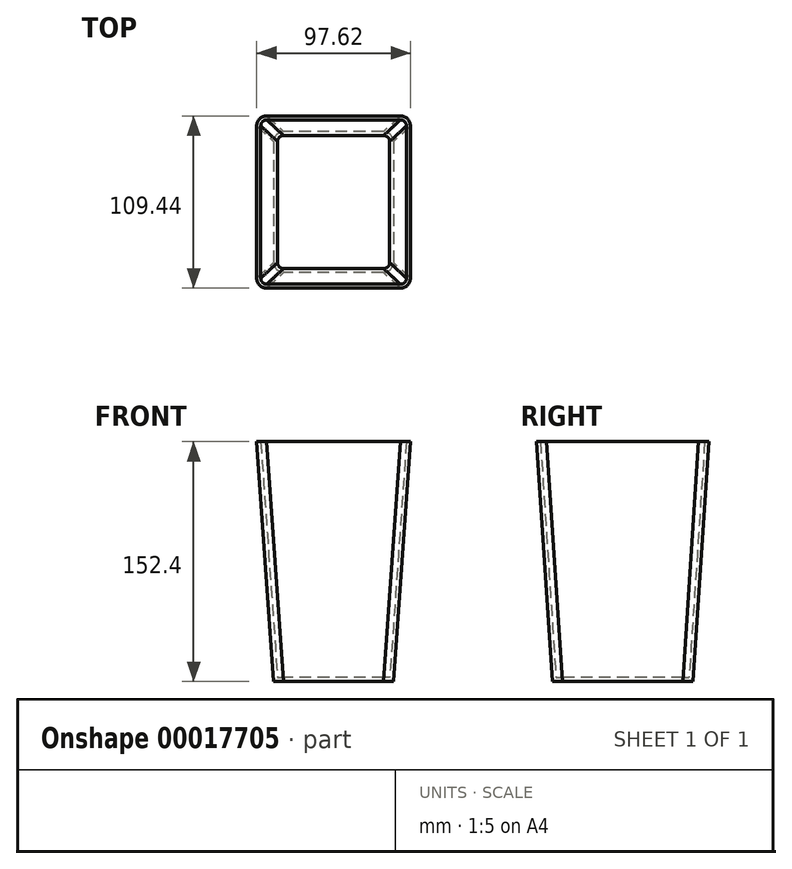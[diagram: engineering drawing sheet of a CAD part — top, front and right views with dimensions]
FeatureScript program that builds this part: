
annotation { "Feature Type Name" : "Feature", "Feature Type Description" : "" }
export const myFeature = defineFeature(function(context is Context, id is Id, definition is map)
    precondition{}
    {
        {
            var Q0;
            Q0=qCreatedBy(makeId("Top.planeOp"),FACE);
            var sketch = newSketch(context, id + "F0", { "sketchPlane" : qUnion([Q0])});
            skLineSegment(sketch, "E0.rect.bottom", {"start": v(31.64, 44.66) * mm, "end": v(-31.64, 44.66) * mm});
            skLineSegment(sketch, "E0.rect.top", {"start": v(31.64, -44.66) * mm, "end": v(-31.64, -44.66) * mm});
            skLineSegment(sketch, "E0.rect.left", {"start": v(38, 38.3) * mm, "end": v(38, -38.3) * mm});
            skLineSegment(sketch, "E0.rect.right", {"start": v(-38, 38.3) * mm, "end": v(-38, -38.3) * mm});
            skPoint(sketch, "E0.rect.middle", {"position": v(0, 0) * mm});
            skPoint(sketch, "E1.visualSharp", {"position": v(-38, 44.66) * mm});
            skArc(sketch, "E1.filletArc", {"start": v(-31.64, 44.66) * mm, "mid": v(-36.13, 42.8) * mm, "end": v(-38, 38.3) * mm});
            skPoint(sketch, "E2.visualSharp", {"position": v(38, 44.66) * mm});
            skArc(sketch, "E2.filletArc", {"start": v(38, 38.3) * mm, "mid": v(36.13, 42.8) * mm, "end": v(31.64, 44.66) * mm});
            skPoint(sketch, "E3.visualSharp", {"position": v(38, -44.66) * mm});
            skArc(sketch, "E3.filletArc", {"start": v(31.64, -44.66) * mm, "mid": v(36.13, -42.8) * mm, "end": v(38, -38.3) * mm});
            skPoint(sketch, "E4.visualSharp", {"position": v(-38, -44.66) * mm});
            skArc(sketch, "E4.filletArc", {"start": v(-38, -38.3) * mm, "mid": v(-36.13, -42.8) * mm, "end": v(-31.64, -44.66) * mm});
            skSolve(sketch);
        }
        {
            var Q0;
            Q0=makeQuery(id+"F0.imprint","IMPRINT",FACE,{"disambiguationData":[TD([[makeQuery(id+"F0.imprint","IMPRINT",EDGE,{"derivedFrom":sQuery(id+"F0.wireOp",EDGE,"E0.rect.bottom")}),1.0]])]});
            cPlane(context, id + "F1", {"entities" : qUnion([Q0]), "cplaneType" : CPlaneType.OFFSET, "offset" : 152.4 * mm, "width" : 152.4 * mm, "height" : 152.4 * mm});
        }
        {
            var Q0;
            Q0=qCreatedBy(id+"F1.planeOp",FACE);
            var sketch = newSketch(context, id + "F2", { "sketchPlane" : qUnion([Q0])});
            skLineSegment(sketch, "E5.rect.bottom", {"start": v(42.46, 54.72) * mm, "end": v(-42.46, 54.72) * mm});
            skLineSegment(sketch, "E5.rect.top", {"start": v(42.46, -54.72) * mm, "end": v(-42.46, -54.72) * mm});
            skLineSegment(sketch, "E5.rect.left", {"start": v(48.81, 48.37) * mm, "end": v(48.81, -48.37) * mm});
            skLineSegment(sketch, "E5.rect.right", {"start": v(-48.81, 48.37) * mm, "end": v(-48.81, -48.37) * mm});
            skPoint(sketch, "E5.rect.middle", {"position": v(0, 0) * mm});
            skPoint(sketch, "E6.visualSharp", {"position": v(-48.81, 54.72) * mm});
            skArc(sketch, "E6.filletArc", {"start": v(-42.46, 54.72) * mm, "mid": v(-46.95, 52.86) * mm, "end": v(-48.81, 48.37) * mm});
            skPoint(sketch, "E7.visualSharp", {"position": v(48.81, 54.72) * mm});
            skArc(sketch, "E7.filletArc", {"start": v(48.81, 48.37) * mm, "mid": v(46.95, 52.86) * mm, "end": v(42.46, 54.72) * mm});
            skPoint(sketch, "E8.visualSharp", {"position": v(48.81, -54.72) * mm});
            skArc(sketch, "E8.filletArc", {"start": v(42.46, -54.72) * mm, "mid": v(46.95, -52.86) * mm, "end": v(48.81, -48.37) * mm});
            skPoint(sketch, "E9.visualSharp", {"position": v(-48.81, -54.72) * mm});
            skArc(sketch, "E9.filletArc", {"start": v(-48.81, -48.37) * mm, "mid": v(-46.95, -52.86) * mm, "end": v(-42.46, -54.72) * mm});
            skSolve(sketch);
        }
        {
            var Q0;
            Q0=makeQuery(id+"F2.imprint","IMPRINT",FACE,{"disambiguationData":[TD([[makeQuery(id+"F2.imprint","IMPRINT",EDGE,{"derivedFrom":sQuery(id+"F2.wireOp",EDGE,"E5.rect.bottom")}),1.0]])]});
            var Q1;
            Q1=makeQuery(id+"F0.imprint","IMPRINT",FACE,{"disambiguationData":[TD([[makeQuery(id+"F0.imprint","IMPRINT",EDGE,{"derivedFrom":sQuery(id+"F0.wireOp",EDGE,"E0.rect.bottom")}),1.0]])]});
            loft(context, id + "F3", {"sheetProfilesArray" : [{ "sheetProfileEntities" : qUnion([Q0]) }, { "sheetProfileEntities" : qUnion([Q1]) }]});
        }
        {
            var Q0;
            Q0=makeQuery(id+"F3.opLoft","CAP_FACE",FACE,{"disambiguationData":[OSD([makeQuery(id+"F2.imprint","IMPRINT",FACE,{"disambiguationData":[TD([[makeQuery(id+"F2.imprint","IMPRINT",EDGE,{"derivedFrom":sQuery(id+"F2.wireOp",EDGE,"E5.rect.bottom")}),1.0]])]})])],"isStart":true});
            shell(context, id + "F4", {"entities" : qUnion([Q0]), "thickness" : 2.54 * mm});
        }
        {
            var Q0;
            Q0=makeQuery(id+"F3.opLoft","SWEPT_FACE",FACE,{"disambiguationData":[OSD([sQuery(id+"F0.wireOp",EDGE,"E0.rect.bottom"),sQuery(id+"F0.wireOp",EDGE,"E1.filletArc"),sQuery(id+"F0.wireOp",EDGE,"E2.filletArc"),sQuery(id+"F2.wireOp",EDGE,"E5.rect.bottom"),sQuery(id+"F2.wireOp",EDGE,"E6.filletArc"),sQuery(id+"F2.wireOp",EDGE,"E7.filletArc")])]});
            var sketch = newSketch(context, id + "F5", { "sketchPlane" : qUnion([Q0])});
            skLineSegment(sketch, "E10.rect.bottom", {"start": v(-19.05, 135.06) * mm, "end": v(19.05, 135.06) * mm});
            skLineSegment(sketch, "E10.rect.top", {"start": v(-19.05, 122.36) * mm, "end": v(19.05, 122.36) * mm});
            skLineSegment(sketch, "E10.rect.left", {"start": v(-19.05, 135.06) * mm, "end": v(-19.05, 122.36) * mm});
            skLineSegment(sketch, "E10.rect.right", {"start": v(19.05, 135.06) * mm, "end": v(19.05, 122.36) * mm});
            skPoint(sketch, "E10.rect.middle", {"position": v(0, 128.7) * mm});
            skLineSegment(sketch, "E11.rect.bottom", {"start": v(19.05, 56.41) * mm, "end": v(-19.05, 56.41) * mm});
            skLineSegment(sketch, "E11.rect.top", {"start": v(19.05, 43.71) * mm, "end": v(-19.05, 43.71) * mm});
            skLineSegment(sketch, "E11.rect.left", {"start": v(19.05, 56.41) * mm, "end": v(19.05, 43.71) * mm});
            skLineSegment(sketch, "E11.rect.right", {"start": v(-19.05, 56.41) * mm, "end": v(-19.05, 43.71) * mm});
            skPoint(sketch, "E11.rect.middle", {"position": v(0, 50.06) * mm});
            skSolve(sketch);
        }
        {
            var Q0;
            Q0=qCreatedBy(makeId("Right.planeOp"),FACE);
            var sketch = newSketch(context, id + "F6", { "sketchPlane" : qUnion([Q0])});
            skFitSpline(sketch, "E12", {"points": [v(47.93, 46.77) * mm, v(79.41, 39.3) * mm, v(102.02, 57.87) * mm, v(101.64, 75.28) * mm, v(96.2, 91.76) * mm, v(88.64, 101.7) * mm, v(75.7, 104.9) * mm, v(63.28, 103) * mm, v(52.24, 106.34) * mm], "startDerivative": vector(187.25, -86) * mm, "endDerivative": vector(-107.67, 48.74) * mm});
            skSolve(sketch);
        }
    });
